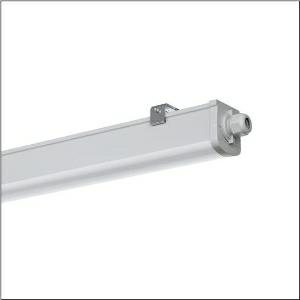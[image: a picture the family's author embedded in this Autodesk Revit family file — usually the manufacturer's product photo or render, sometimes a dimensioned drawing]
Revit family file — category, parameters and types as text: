
# Revit family: monsun_r__31_51fa207p460b_ddf4
name_source: partatom
category: Lighting Fixtures
units: mm (PartAtom-declared; Revit-internal decimal feet)

## family parameters
Cut with Voids When Loaded = No
Host = Face
Light Source = No
Part Type = Normal
Room Calculation Point = No
Round Connector Dimension = Use Diameter
Shared = No

## types (1)
- Monsun® 31 (1 x LED, 6700 lm, 50 W, 4000K)
    Apparent Load = 50 VA
    CIE Flux Codes = 42 72 91 92 100
    Color Rendering = 80
    Color Temperature = 4000K
    Default Elevation = 1800 mm
    Description = Monsun® 31, damp-proof luminaire, primary optical cover: diffuser, of PC, frosted, light emission: direct distribution, primary light characteristic: symmetric, installation type: surface-mounted, LED, rated luminous flux: 6.700lm, luminous efficacy: 134lm/W, light colour: 840, colour temperature: 4000K, control gear: ECG, with terminal, 3+1-pole, max. 2.5mm², through-wiring: 3x 2.5mm² + 1x 1.5mm², mains connection: 220..240V, AC, 50/60Hz, rated input power: 50W, housing, luminaire housing, of PC, light grey (RAL 7035), length: 1.458mm, width: 68mm, height: 76mm, protection rating (complete): IP66, insulation class (complete): insulation class II (safety insulation), certification: CE, ENEC, UKCA, protection symbol: D, impact resistance: IK08, permissible operating ambient temperature: -20..+40°C, corresponds to IFS (International Featured Standards) requirements for safety and quality in the food industry, packaging unit: 1 piece
    Height = 77 mm
    Lamp = 1 x LED
    Lamp Light Flux = 6700 lm
    Lamp Power = 50 W
    Lamp count = 1
    Length = 1518 mm
    Luminous efficacy = 134 lm/W
    Manufacturer = Siteco
    ModVariant = No
    Model = 51FA207P460B
    Mounting Place = Ceiling
    Mounting Type = Surface mounted
    Number of Poles = 1
    OnlyDefault = Yes
    Power Factor = 1
    Product Name = Monsun® 31
    Product group = damp-proof luminaire | ceiling mounted
    ProductGroupID = 300
    Protection Class = Protection class II
    Protection Degree = IP 66
    RLX_Detail_Level = 1
    RlxData = <blob elided: 33065 chars, md5=16adfe29>
    Socket = socket
    Standby Power = 0 W
    System Light Flux = 6700 lm
    System Power = 50 W
    Type Comments = Product without accessories
    Type Image = l_1006174.jpg
    URL = http://relux.com
    VarID = ---
    Voltage = 0 V
    Weight = 0.00 kg
    Width = 69 mm

## geometry (parser evidence)
native form markers: Blend x4, Sweep x11
no freeform markers — native parametric forms only
